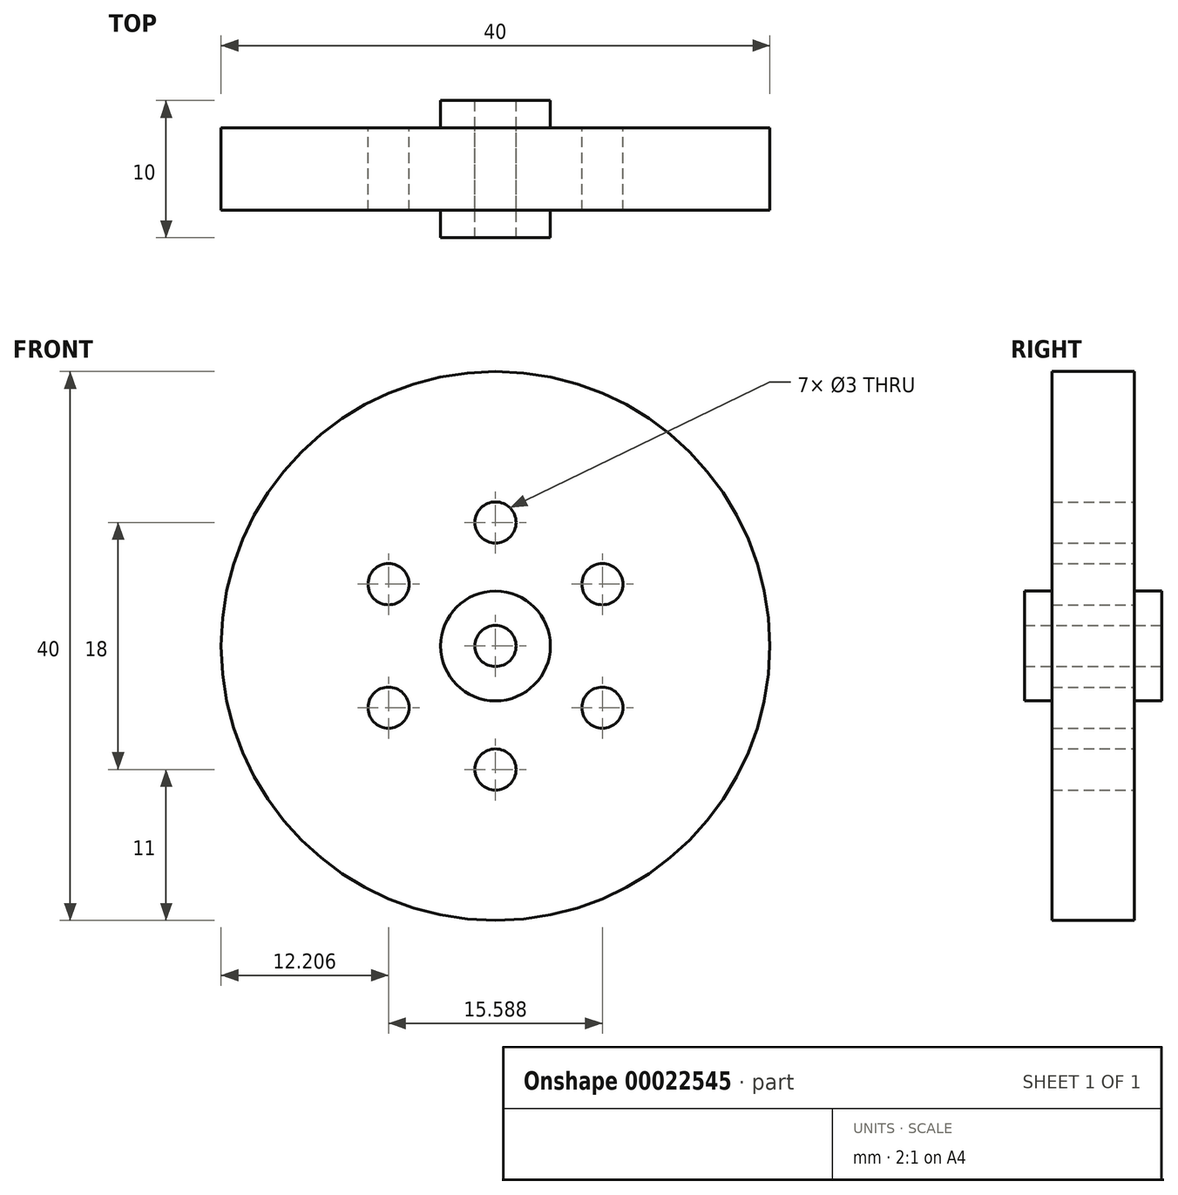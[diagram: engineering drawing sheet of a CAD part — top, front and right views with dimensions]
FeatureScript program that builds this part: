
annotation { "Feature Type Name" : "Feature", "Feature Type Description" : "" }
export const myFeature = defineFeature(function(context is Context, id is Id, definition is map)
    precondition{}
    {
        {
            var Q0;
            Q0=qCreatedBy(makeId("Front.planeOp"),FACE);
            var sketch = newSketch(context, id + "F0", { "sketchPlane" : qUnion([Q0])});
            skCircle(sketch, "E0", {"center": v(0, 0) * mm, "radius": 20 * mm});
            skCircle(sketch, "E1", {"center": v(0, 0) * mm, "radius": 4 * mm});
            skCircle(sketch, "E2", {"center": v(0, 0) * mm, "radius": 1.5 * mm});
            skCircle(sketch, "E3", {"center": v(0, 9) * mm, "radius": 1.5 * mm});
            skCircle(sketch, "E4.1.0", {"center": v(-7.8, 4.5) * mm, "radius": 1.5 * mm});
            skCircle(sketch, "E4.2.0", {"center": v(-7.8, -4.5) * mm, "radius": 1.5 * mm});
            skCircle(sketch, "E4.3.0", {"center": v(0, -9) * mm, "radius": 1.5 * mm});
            skCircle(sketch, "E4.4.0", {"center": v(7.8, -4.5) * mm, "radius": 1.5 * mm});
            skCircle(sketch, "E4.5.0", {"center": v(7.8, 4.5) * mm, "radius": 1.5 * mm});
            skSolve(sketch);
        }
        {
            var Q0;
            Q0=makeQuery(id+"F0.imprint","IMPRINT",FACE,{"disambiguationData":[TD([[makeQuery(id+"F0.imprint","IMPRINT",EDGE,{"derivedFrom":sQuery(id+"F0.wireOp",EDGE,"E0")}),1.0]])]});
            extrude(context, id + "F1", {"entities" : qUnion([Q0]), "depth" : 6 * mm});
        }
        {
            var Q0;
            Q0=makeQuery(id+"F0.imprint","IMPRINT",FACE,{"disambiguationData":[TD([[makeQuery(id+"F0.imprint","IMPRINT",EDGE,{"derivedFrom":sQuery(id+"F0.wireOp",EDGE,"E1")}),1.0]])]});
            extrude(context, id + "F2", {"entities" : qUnion([Q0]), "operationType" : NewBodyOperationType.ADD, "depth" : 8 * mm});
        }
        {
            var Q0;
            {var subQ0=sQuery(id+"F0.wireOp",EDGE,"E1");Q0=makeQuery(id+"F2.boolean.opBoolean","MERGE",FACE,{"derivedFrom":[makeQuery(id+"F1.opExtrude","CAP_FACE",FACE,{"disambiguationData":[OSD([sQuery(id+"F0.wireOp",EDGE,"E0"),subQ0,sQuery(id+"F0.wireOp",EDGE,"E3"),sQuery(id+"F0.wireOp",EDGE,"E4.1.0"),sQuery(id+"F0.wireOp",EDGE,"E4.2.0"),sQuery(id+"F0.wireOp",EDGE,"E4.3.0"),sQuery(id+"F0.wireOp",EDGE,"E4.4.0"),sQuery(id+"F0.wireOp",EDGE,"E4.5.0")])],"isStart":true}),makeQuery(id+"F2.opExtrude","CAP_FACE",FACE,{"disambiguationData":[OSD([subQ0,sQuery(id+"F0.wireOp",EDGE,"E2")])],"isStart":true})]});}
            var sketch = newSketch(context, id + "F3", { "sketchPlane" : qUnion([Q0])});
            skCircle(sketch, "E5", {"center": v(0, 0) * mm, "radius": 4 * mm});
            skSolve(sketch);
        }
        {
            var Q0;
            Q0=makeQuery(id+"F3.imprint","IMPRINT",FACE,{"disambiguationData":[TD([[makeQuery(id+"F3.imprint","IMPRINT",EDGE,{"derivedFrom":sQuery(id+"F3.wireOp",EDGE,"E5")}),1.0]])]});
            extrude(context, id + "F4", {"entities" : qUnion([Q0]), "operationType" : NewBodyOperationType.ADD, "depth" : 2 * mm});
        }
    });
